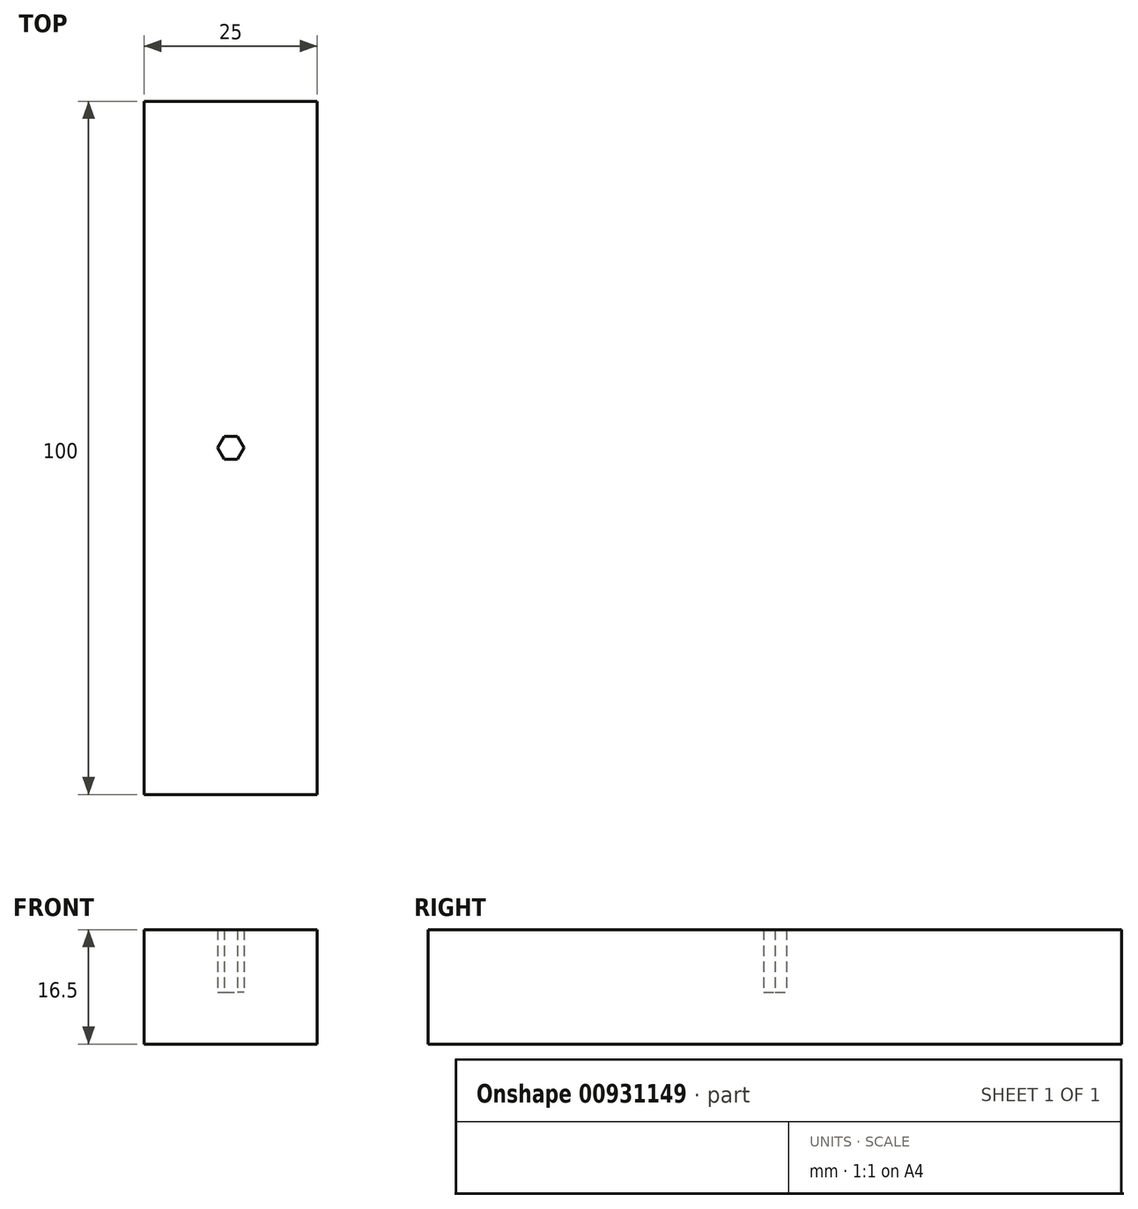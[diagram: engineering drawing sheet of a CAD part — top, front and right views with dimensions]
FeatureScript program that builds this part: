
annotation { "Feature Type Name" : "Feature", "Feature Type Description" : "" }
export const myFeature = defineFeature(function(context is Context, id is Id, definition is map)
    precondition{}
    {
        {
            assignVariable(context, id + "F0", {"name" : "HexSize", "anyValue" : 3 * mm});
        }
        {
            assignVariable(context, id + "F1", {"name" : "BottomThickness", "anyValue" : 7.5 * mm});
        }
        {
            assignVariable(context, id + "F2", {"name" : "InsertionDepth", "anyValue" : getVariable(context, 'HexSize') * 3});
        }
        {
            assignVariable(context, id + "F3", {"name" : "BlockHeight", "anyValue" : getVariable(context, 'BottomThickness') + getVariable(context, 'InsertionDepth')});
        }
        {
            var Q0;
            Q0=qCreatedBy(makeId("Top.planeOp"),FACE);
            var sketch = newSketch(context, id + "F4", { "sketchPlane" : qUnion([Q0])});
            skLineSegment(sketch, "E0.bottom", {"start": v(-12.5, -50) * mm, "end": v(12.5, -50) * mm});
            skLineSegment(sketch, "E0.top", {"start": v(-12.5, 50) * mm, "end": v(12.5, 50) * mm});
            skLineSegment(sketch, "E0.left", {"start": v(-12.5, -50) * mm, "end": v(-12.5, 50) * mm});
            skLineSegment(sketch, "E0.right", {"start": v(12.5, -50) * mm, "end": v(12.5, 50) * mm});
            skSolve(sketch);
        }
        {
            var Q0;
            Q0=makeQuery(id+"F4.imprint","IMPRINT",FACE,{"disambiguationData":[TD([[makeQuery(id+"F4.imprint","IMPRINT",EDGE,{"derivedFrom":sQuery(id+"F4.wireOp",EDGE,"E0.bottom")}),1.0]])]});
            extrude(context, id + "F5", {"entities" : qUnion([Q0]), "depth" : getVariable(context, 'BlockHeight'), "offsetDistance" : 25 * mm});
        }
        {
            var Q0;
            Q0=qCreatedBy(makeId("Top.planeOp"),FACE);
            var sketch = newSketch(context, id + "F6", { "sketchPlane" : qUnion([Q0])});
            skCircle(sketch, "E1.cCircle", {"center": v(0, 0) * mm, "radius": 1.65 * mm, "construction": true});
            skLineSegment(sketch, "E1.0", {"start": v(-0.95, 1.65) * mm, "end": v(0.95, 1.65) * mm});
            skLineSegment(sketch, "E1.1", {"start": v(0.95, 1.65) * mm, "end": v(1.9, 0) * mm});
            skLineSegment(sketch, "E1.2", {"start": v(1.9, 0) * mm, "end": v(0.95, -1.65) * mm});
            skLineSegment(sketch, "E1.3", {"start": v(0.95, -1.65) * mm, "end": v(-0.95, -1.65) * mm});
            skLineSegment(sketch, "E1.4", {"start": v(-0.95, -1.65) * mm, "end": v(-1.9, 0) * mm});
            skLineSegment(sketch, "E1.5", {"start": v(-1.9, 0) * mm, "end": v(-0.95, 1.65) * mm});
            skPoint(sketch, "E1.0.midPoint", {"position": v(0, 1.65) * mm});
            skLineSegment(sketch, "E2", {"start": v(0, -2.83) * mm, "end": v(0, 3.35) * mm, "construction": true});
            skLineSegment(sketch, "E3", {"start": v(-3.68, 0) * mm, "end": v(4.03, 0) * mm, "construction": true});
            skLineSegment(sketch, "E4.bottom", {"start": v(-12.5, -50) * mm, "end": v(12.5, -50) * mm});
            skLineSegment(sketch, "E4.top", {"start": v(-12.5, 50) * mm, "end": v(12.5, 50) * mm});
            skLineSegment(sketch, "E4.left", {"start": v(-12.5, -50) * mm, "end": v(-12.5, 50) * mm});
            skLineSegment(sketch, "E4.right", {"start": v(12.5, -50) * mm, "end": v(12.5, 50) * mm});
            skSolve(sketch);
        }
        {
            var Q0;
            Q0=makeQuery(id+"F6.imprint","IMPRINT",FACE,{"disambiguationData":[TD([[makeQuery(id+"F6.imprint","IMPRINT",EDGE,{"derivedFrom":sQuery(id+"F6.wireOp",EDGE,"E1.0")}),-1.0]])]});
            extrude(context, id + "F7", {"entities" : qUnion([Q0]), "operationType" : NewBodyOperationType.REMOVE, "depth" : getVariable(context, 'BlockHeight'), "offsetDistance" : 25 * mm, "hasSecondDirection" : true, "secondDirectionOppositeDirection" : false, "secondDirectionDepth" : getVariable(context, 'BottomThickness')});
        }
    });
